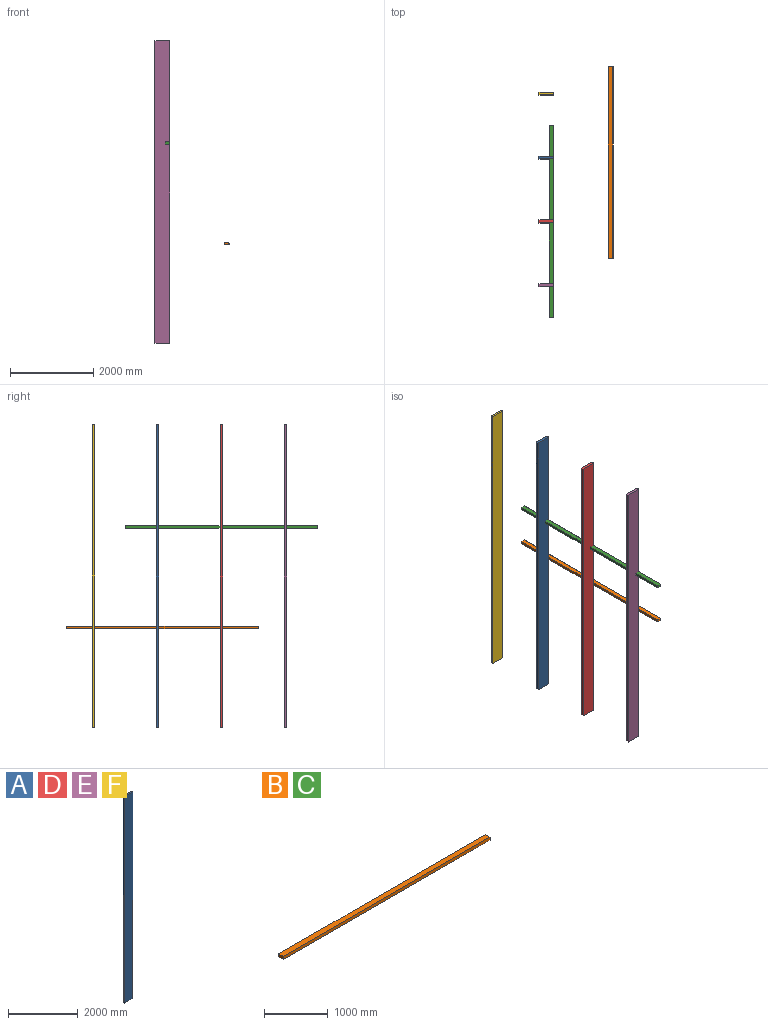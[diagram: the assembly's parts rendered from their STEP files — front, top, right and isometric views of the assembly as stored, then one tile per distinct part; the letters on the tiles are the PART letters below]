
ASSEMBLY  parts=6 mates=5
PART A: 10 faces, bbox 360x60x7250 mm
  f0: plane 7250x20.5mm, normal (1,0,0), area 148625mm2, adj f1,f7,f8,f9
  f1: plane 7250x18mm, normal (0,-1,0), area 130500mm2, adj f0,f2,f8,f9
  f2: plane 7250x19mm, normal (1,0,0), area 137750mm2, adj f1,f3,f8,f9
  f3: plane 7250x18mm, normal (0,1,0), area 130500mm2, adj f2,f4,f8,f9
  f4: plane 7250x20.5mm, normal (1,0,0), area 148625mm2, adj f3,f5,f8,f9
  f5: plane 7250x342mm, normal (0,1,0), area 2479500mm2, adj f4,f6,f8,f9
  f6: plane 7250x60mm, normal (-1,0,0), area 435000mm2, adj f5,f7,f8,f9
  f7: plane 7250x342mm, normal (0,-1,0), area 2479500mm2, adj f0,f6,f8,f9
  f8: plane 360x60mm, normal (0,0,1), area 20862mm2, adj f0,f1,f2,f3,f4,f5,f6,f7
  f9: plane 360x60mm, normal (0,0,-1), area 20862mm2, adj f0,f1,f2,f3,f4,f5,f6,f7
PART B: 10 faces, bbox 4600x118x60 mm
  f0: plane 4600x20.5mm, normal (0,1,0), area 94300mm2, adj f1,f7,f8,f9
  f1: plane 4600x18mm, normal (0,0,-1), area 82800mm2, adj f0,f2,f8,f9
  f2: plane 4600x19mm, normal (0,1,0), area 87400mm2, adj f1,f3,f8,f9
  f3: plane 4600x18mm, normal (0,0,1), area 82800mm2, adj f2,f4,f8,f9
  f4: plane 4600x20.5mm, normal (0,1,0), area 94300mm2, adj f3,f5,f8,f9
  f5: plane 4600x100mm, normal (0,0,1), area 460000mm2, adj f4,f6,f8,f9
  f6: plane 4600x60mm, normal (0,-1,0), area 276000mm2, adj f5,f7,f8,f9
  f7: plane 4600x100mm, normal (0,0,-1), area 460000mm2, adj f0,f6,f8,f9
  f8: plane 118x60mm, normal (1,0,0), area 6342mm2, adj f0,f1,f2,f3,f4,f5,f6,f7
  f9: plane 118x60mm, normal (-1,0,0), area 6342mm2, adj f0,f1,f2,f3,f4,f5,f6,f7
PART C: same geometry as B
PART D: same geometry as A
PART E: same geometry as A
PART F: same geometry as A
PLACE A t=(-2857.85,-3463.25,-7356.48)mm
PLACE B rot(axis=(0,0,-1),90deg) t=(-1200.57,-1311.25,-4939.8)mm
PLACE C rot(axis=(0,0,-1),90deg) t=(-2615.9,-2726.58,-2523.14)mm
PLACE D t=(-2857.85,-4996.58,-7356.48)mm
PLACE E t=(-2857.85,-6529.91,-7356.48)mm
PLACE F t=(-2857.85,-1929.92,-7356.48)mm
MATE parallel F.f8 <-> A.f8  axis (0,0,1) through (-2683.9,-1959.92,-106.48)mm
MATE parallel C.f5 <-> A.f8  axis (0,0,1) through (-2565.9,-5026.58,-2523.14)mm
MATE parallel D.f8 <-> E.f8  axis (0,0,1) through (-2683.9,-5026.58,-106.48)mm
MATE parallel A.f8 <-> D.f8  axis (0,0,1) through (-2683.9,-3493.25,-106.48)mm
MATE parallel B.f5 <-> A.f8  axis (0,0,1) through (-1150.57,-3611.25,-4939.8)mm
